# Revit family: 3P-SURFACE MOUNTED
name_source: partatom
category: Air Terminals
revit_build: Autodesk Revit 2018 (Build: 20170223_1515(x64)
units: mm (PartAtom-declared; Revit-internal decimal feet)

## family parameters
Always vertical = Yes
Cut with Voids When Loaded = No
OmniClass Number = 23.75.00.00
OmniClass Title = Climate Control (HVAC)
Part Type = Normal
Room Calculation Point = No
Round Connector Dimension = Use Diameter
Shared = No
Work Plane-Based = No

## types (2) — shared parameters
Angle120 = 120.00°
Description = PERFORATED RETURN
FINISH = ARCTIC WHITE
Frame Flangeup = 0' - 0 3/16"
Frame Width = 0' - 1 7/32"
FrameNeck = 0' - 0 25/32"
Manufacturer = ANEMOSTAT
Maximum Size = 83' - 3"
Minimum Size = 0' - 4"
Model = 3P
Neck Clearance = 0' - 0 1/8"
Neck Height = 0' - 1 3/32"
Nose.087 = 0' - 0 1/8"
Offset3/16 = 0' - 0 3/16"
Offset313 = 0' - 0 5/16"
Offset585 = 0' - 0 19/32"
Offset7/16 = 0' - 0 7/16"
Thickness = 0' - 0 1/16"
Toe110 = 0' - 0 1/8"
URL = https://www.anemostat-hvac.com
Up256 = 0' - 0 1/4"

## per-type parameters (varying)
| type | MATERIAL |
| 3P-SURFACE MOUNTED, ALUM, DUCT SIZE FROM 4" TO 999" | PERFORATED FACE IN ALUMINUM |
| 3P-SURFACE MOUNTED, STEEL, DUCT SIZE FROM 4" TO 999" | PERFORATED FACE IN STEEL |

## geometry (parser evidence)
native form markers: Sweep x2
no freeform markers — native parametric forms only
